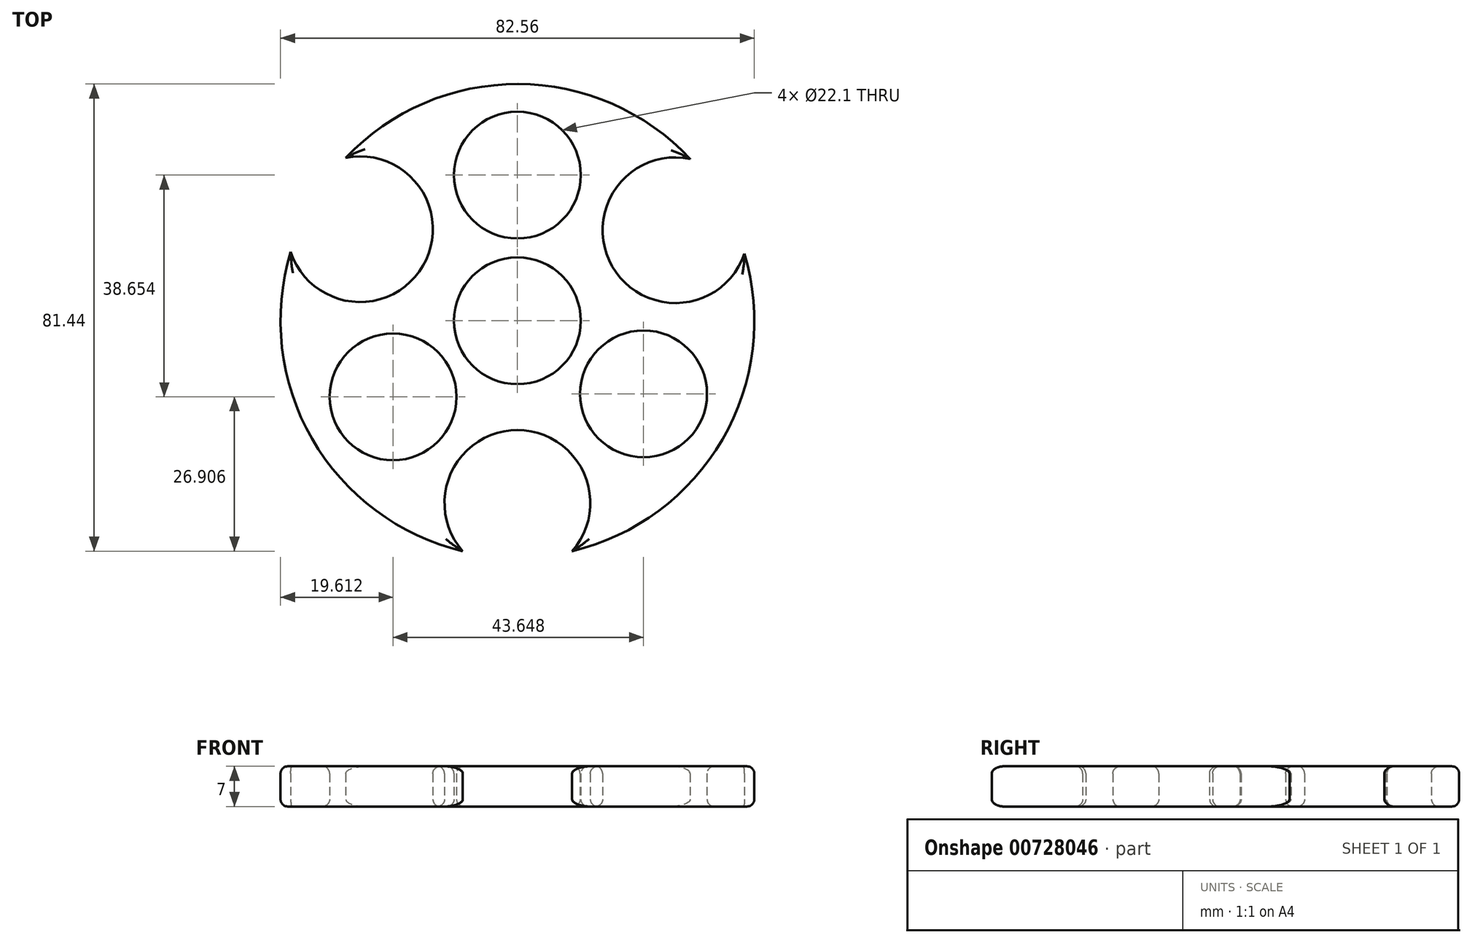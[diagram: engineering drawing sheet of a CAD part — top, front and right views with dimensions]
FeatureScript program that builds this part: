
annotation { "Feature Type Name" : "Feature", "Feature Type Description" : "" }
export const myFeature = defineFeature(function(context is Context, id is Id, definition is map)
    precondition{}
    {
        {
            var Q0;
            Q0=qCreatedBy(makeId("Top.planeOp"),FACE);
            var sketch = newSketch(context, id + "F0", { "sketchPlane" : qUnion([Q0])});
            skCircle(sketch, "E0", {"center": v(0, 0) * mm, "radius": 41.28 * mm});
            skCircle(sketch, "E1.cCircle", {"center": v(0, 0) * mm, "radius": 33.1 * mm, "construction": true});
            skLineSegment(sketch, "E1.0", {"start": v(28.69, -16.51) * mm, "end": v(-28.65, -16.59) * mm});
            skLineSegment(sketch, "E1.1", {"start": v(-28.65, -16.59) * mm, "end": v(-0.04, 33.1) * mm});
            skLineSegment(sketch, "E1.2", {"start": v(-0.04, 33.1) * mm, "end": v(28.69, -16.51) * mm});
            skSolve(sketch);
        }
        {
            var Q0;
            Q0=makeQuery(id+"F0.imprint","IMPRINT",FACE,{"disambiguationData":[TD([[makeQuery(id+"F0.imprint","IMPRINT",EDGE,{"derivedFrom":sQuery(id+"F0.wireOp",EDGE,"E0")}),1.0]])]});
            var sketch = newSketch(context, id + "F1", { "sketchPlane" : qUnion([Q0])});
            skCircle(sketch, "E2", {"center": v(0, 25.4) * mm, "radius": 11.05 * mm});
            skCircle(sketch, "E3", {"center": v(-21.67, -13.25) * mm, "radius": 11.05 * mm});
            skCircle(sketch, "E4", {"center": v(21.98, -12.73) * mm, "radius": 11.05 * mm});
            skCircle(sketch, "E5", {"center": v(0, 0) * mm, "radius": 11.05 * mm});
            skSolve(sketch);
        }
        {
            var Q0;
            Q0=makeQuery(id+"F0.imprint","IMPRINT",FACE,{"disambiguationData":[TD([[makeQuery(id+"F0.imprint","IMPRINT",EDGE,{"derivedFrom":sQuery(id+"F0.wireOp",EDGE,"E0")}),1.0]])]});
            var Q1;
            Q1=makeQuery(id+"F0.imprint","IMPRINT",FACE,{"disambiguationData":[TD([[makeQuery(id+"F0.imprint","IMPRINT",EDGE,{"derivedFrom":sQuery(id+"F0.wireOp",EDGE,"E1.0")}),-1.0]])]});
            extrude(context, id + "F2", {"entities" : qUnion([Q0, Q1]), "depth" : 7 * mm, "offsetDistance" : 25.4 * mm});
        }
        {
            var Q0;
            {var subQ0=sQuery(id+"F1.wireOp",EDGE,"E4");var subQ1=makeQuery(id+"F0.imprint","IMPRINT",EDGE,{"derivedFrom":sQuery(id+"F0.wireOp",EDGE,"E1.0")});var subQ2=makeQuery(id+"F1.imprint","INTERSECT",VERTEX,{"derivedFrom":[subQ1,subQ0]});Q0=makeQuery(id+"F1.imprint","IMPRINT",FACE,{"disambiguationData":[TD([[makeQuery(id+"F1.imprint","IMPRINT",EDGE,{"disambiguationData":[TD([[subQ2,1.0]])],"derivedFrom":subQ0}),1.0]])]});}
            var Q1;
            {var subQ0=sQuery(id+"F1.wireOp",EDGE,"E4");var subQ1=makeQuery(id+"F0.imprint","IMPRINT",EDGE,{"derivedFrom":sQuery(id+"F0.wireOp",EDGE,"E1.0")});var subQ2=makeQuery(id+"F1.imprint","INTERSECT",VERTEX,{"derivedFrom":[subQ1,subQ0]});Q1=makeQuery(id+"F1.imprint","IMPRINT",FACE,{"disambiguationData":[TD([[makeQuery(id+"F1.imprint","IMPRINT",EDGE,{"disambiguationData":[TD([[subQ2,-1.0]])],"derivedFrom":subQ0}),1.0]])]});}
            var Q2;
            Q2=makeQuery(id+"F1.imprint","IMPRINT",FACE,{"disambiguationData":[TD([[makeQuery(id+"F1.imprint","IMPRINT",EDGE,{"derivedFrom":sQuery(id+"F1.wireOp",EDGE,"E5")}),1.0]])]});
            var Q3;
            {var subQ0=sQuery(id+"F1.wireOp",EDGE,"E3");var subQ1=makeQuery(id+"F0.imprint","IMPRINT",EDGE,{"derivedFrom":sQuery(id+"F0.wireOp",EDGE,"E1.0")});var subQ2=makeQuery(id+"F1.imprint","INTERSECT",VERTEX,{"derivedFrom":[subQ1,subQ0]});Q3=makeQuery(id+"F1.imprint","IMPRINT",FACE,{"disambiguationData":[TD([[makeQuery(id+"F1.imprint","IMPRINT",EDGE,{"disambiguationData":[TD([[subQ2,1.0]])],"derivedFrom":subQ0}),1.0]])]});}
            var Q4;
            {var subQ0=sQuery(id+"F1.wireOp",EDGE,"E3");var subQ1=makeQuery(id+"F0.imprint","IMPRINT",EDGE,{"derivedFrom":sQuery(id+"F0.wireOp",EDGE,"E1.0")});var subQ2=makeQuery(id+"F1.imprint","INTERSECT",VERTEX,{"derivedFrom":[subQ1,subQ0]});Q4=makeQuery(id+"F1.imprint","IMPRINT",FACE,{"disambiguationData":[TD([[makeQuery(id+"F1.imprint","IMPRINT",EDGE,{"disambiguationData":[TD([[subQ2,-1.0]])],"derivedFrom":subQ0}),1.0]])]});}
            var Q5;
            {var subQ0=sQuery(id+"F1.wireOp",EDGE,"E2");var subQ1=makeQuery(id+"F0.imprint","IMPRINT",EDGE,{"derivedFrom":sQuery(id+"F0.wireOp",EDGE,"E1.1")});var subQ2=makeQuery(id+"F1.imprint","INTERSECT",VERTEX,{"derivedFrom":[subQ1,subQ0]});Q5=makeQuery(id+"F1.imprint","IMPRINT",FACE,{"disambiguationData":[TD([[makeQuery(id+"F1.imprint","IMPRINT",EDGE,{"disambiguationData":[TD([[subQ2,-1.0]])],"derivedFrom":subQ0}),1.0]])]});}
            var Q6;
            {var subQ0=sQuery(id+"F1.wireOp",EDGE,"E2");var subQ1=makeQuery(id+"F0.imprint","IMPRINT",EDGE,{"derivedFrom":sQuery(id+"F0.wireOp",EDGE,"E1.1")});var subQ2=makeQuery(id+"F1.imprint","INTERSECT",VERTEX,{"derivedFrom":[subQ1,subQ0]});Q6=makeQuery(id+"F1.imprint","IMPRINT",FACE,{"disambiguationData":[TD([[makeQuery(id+"F1.imprint","IMPRINT",EDGE,{"disambiguationData":[TD([[subQ2,1.0]])],"derivedFrom":subQ0}),1.0]])]});}
            var Q7;
            Q7=sQuery(id+"F1.wireOp",EDGE,"E2");
            var Q8;
            Q8=sQuery(id+"F1.wireOp",EDGE,"E5");
            var Q9;
            Q9=sQuery(id+"F1.wireOp",EDGE,"E3");
            var Q10;
            Q10=sQuery(id+"F1.wireOp",EDGE,"E4");
            extrude(context, id + "F3", {"entities" : qUnion([Q0, Q1, Q2, Q3, Q4, Q5, Q6]), "operationType" : NewBodyOperationType.REMOVE, "surfaceEntities" : qUnion([Q7, Q8, Q9, Q10]), "depth" : 7 * mm, "offsetDistance" : 25.4 * mm});
        }
        {
            var Q0;
            Q0=qCreatedBy(makeId("Top.planeOp"),FACE);
            var sketch = newSketch(context, id + "F4", { "sketchPlane" : qUnion([Q0])});
            skArc(sketch, "E6", {"start": v(-34, 5.1) * mm, "mid": v(-16.52, 9.5) * mm, "end": v(-21.03, 26.95) * mm});
            skArc(sketch, "E7", {"start": v(22.12, 27.29) * mm, "mid": v(16.35, 9.8) * mm, "end": v(34.11, 4.93) * mm});
            skArc(sketch, "E8", {"start": v(12.62, -33.18) * mm, "mid": v(0.76, -19.07) * mm, "end": v(-12.7, -31.67) * mm});
            skSolve(sketch);
        }
        {
            var Q0;
            Q0=sQuery(id+"F4.wireOp",VERTEX,"E6.center");
            var Q1;
            Q1=sQuery(id+"F4.wireOp",VERTEX,"E7.center");
            var Q2;
            Q2=sQuery(id+"F4.wireOp",VERTEX,"E8.center");
            var Q3;
            Q3=makeQuery(id+"F2.opExtrude","SWEPT_BODY",BODY,{"disambiguationData":[OSD([sQuery(id+"F0.wireOp",EDGE,"E0")])]});
            hole(context, id + "F5", {"style" : HoleStyle.SIMPLE, "endStyle" : HoleEndStyle.THROUGH, "oppositeDirection" : true, "holeDiameter" : 25.4 * mm, "majorDiameter" : 6.35 * mm, "isTappedThrough" : true, "tappedDepth" : 12.7 * mm, "tapClearance" : 3, "startFromSketch" : true, "locations" : qUnion([Q0, Q1, Q2]), "scope" : qUnion([Q3])});
        }
        {
            var Q0;
            Q0=makeQuery(id+"F2.opExtrude","CAP_FACE",FACE,{"disambiguationData":[OSD([sQuery(id+"F0.wireOp",EDGE,"E0")])],"isStart":false});
            fillet(context, id + "F6", {"entities" : qUnion([Q0]), "radius" : 1.27 * mm, "tangentPropagation" : true, "allowEdgeOverflow" : false});
        }
        {
            var Q0;
            Q0=makeQuery(id+"F2.opExtrude","CAP_FACE",FACE,{"disambiguationData":[OSD([sQuery(id+"F0.wireOp",EDGE,"E0")])],"isStart":true});
            fillet(context, id + "F7", {"entities" : qUnion([Q0]), "radius" : 1.27 * mm, "tangentPropagation" : true, "allowEdgeOverflow" : false});
        }
    });
